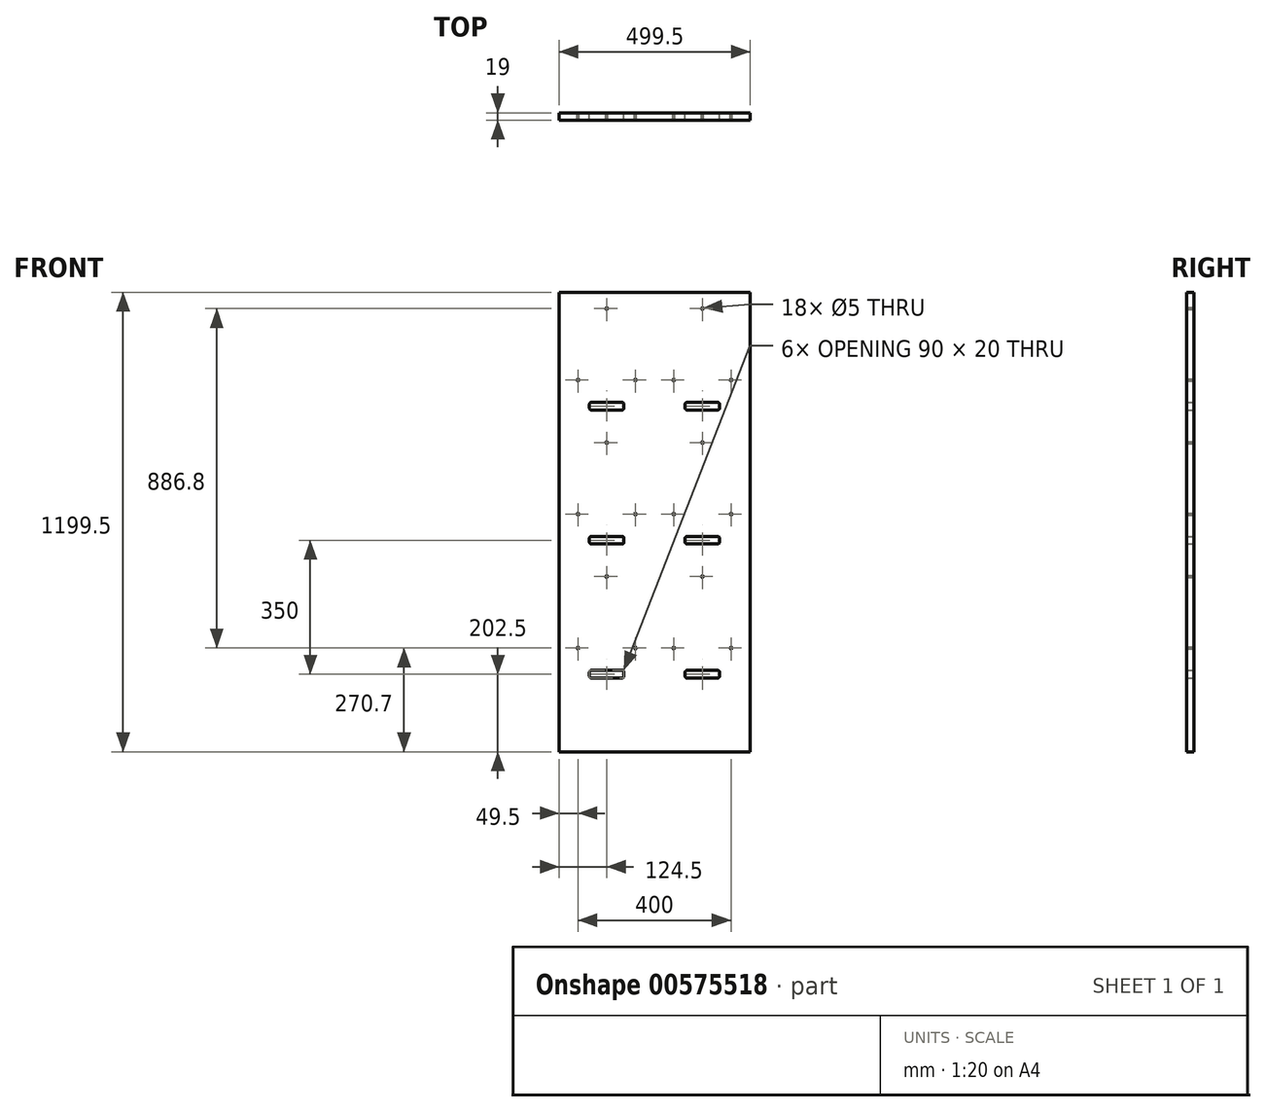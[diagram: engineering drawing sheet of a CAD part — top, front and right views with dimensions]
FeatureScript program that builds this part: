
annotation { "Feature Type Name" : "Feature", "Feature Type Description" : "" }
export const myFeature = defineFeature(function(context is Context, id is Id, definition is map)
    precondition{}
    {
        {
            var Q0;
            Q0=qCreatedBy(makeId("Front.planeOp"),FACE);
            var sketch = newSketch(context, id + "F0", { "sketchPlane" : qUnion([Q0])});
            skLineSegment(sketch, "E0.bottom", {"start": v(0, 0) * mm, "end": v(1000, 0) * mm, "construction": true});
            skLineSegment(sketch, "E0.left", {"start": v(0, 0) * mm, "end": v(0, 1590) * mm, "construction": true});
            skLineSegment(sketch, "E0.right", {"start": v(1000, 0) * mm, "end": v(1000, 1590) * mm, "construction": true});
            skLineSegment(sketch, "E1", {"start": v(500, 1590) * mm, "end": v(500, 0) * mm, "construction": true});
            skLineSegment(sketch, "E2.bottom", {"start": v(0, 1590) * mm, "end": v(1000, 1590) * mm, "construction": true});
            skLineSegment(sketch, "E2.left", {"start": v(0, 1590) * mm, "end": v(0, 290) * mm, "construction": true});
            skSolve(sketch);
        }
        {
            var Q0;
            Q0=qCreatedBy(makeId("Front.planeOp"),FACE);
            var sketch = newSketch(context, id + "F1", { "sketchPlane" : qUnion([Q0])});
            skLineSegment(sketch, "E3.bottom", {"start": v(0, 1590) * mm, "end": v(499.5, 1590) * mm});
            skLineSegment(sketch, "E3.top", {"start": v(0, 390.5) * mm, "end": v(499.5, 390.5) * mm});
            skLineSegment(sketch, "E3.left", {"start": v(0, 1590) * mm, "end": v(0, 390.5) * mm});
            skLineSegment(sketch, "E3.right", {"start": v(499.5, 1590) * mm, "end": v(499.5, 390.5) * mm});
            skLineSegment(sketch, "E4", {"start": v(125, 1590) * mm, "end": v(125, 390.5) * mm, "construction": true});
            skLineSegment(sketch, "E5", {"start": v(375, 1590) * mm, "end": v(375, 390.5) * mm, "construction": true});
            skCircle(sketch, "E6", {"center": v(125, 1548) * mm, "radius": 2.5 * mm});
            skCircle(sketch, "E7", {"center": v(50, 1361.2) * mm, "radius": 2.5 * mm});
            skCircle(sketch, "E8.MirrorC", {"center": v(200, 1361.2) * mm, "radius": 2.5 * mm});
            skLineSegment(sketch, "E9.bottom", {"start": v(165, 1283) * mm, "end": v(85, 1283) * mm});
            skLineSegment(sketch, "E9.top", {"start": v(165, 1303) * mm, "end": v(85, 1303) * mm});
            skLineSegment(sketch, "E9.left", {"start": v(170, 1288) * mm, "end": v(170, 1298) * mm});
            skLineSegment(sketch, "E9.right", {"start": v(80, 1288) * mm, "end": v(80, 1298) * mm});
            skPoint(sketch, "E9.middle", {"position": v(125, 1293) * mm});
            skPoint(sketch, "E10.visualSharp", {"position": v(80, 1303) * mm});
            skArc(sketch, "E10.filletArc", {"start": v(85, 1303) * mm, "mid": v(81.46, 1301.54) * mm, "end": v(80, 1298) * mm});
            skPoint(sketch, "E11.visualSharp", {"position": v(80, 1283) * mm});
            skArc(sketch, "E11.filletArc", {"start": v(80, 1288) * mm, "mid": v(81.46, 1284.46) * mm, "end": v(85, 1283) * mm});
            skPoint(sketch, "E12.visualSharp", {"position": v(170, 1283) * mm});
            skArc(sketch, "E12.filletArc", {"start": v(165, 1283) * mm, "mid": v(168.54, 1284.46) * mm, "end": v(170, 1288) * mm});
            skPoint(sketch, "E13.visualSharp", {"position": v(170, 1303) * mm});
            skArc(sketch, "E13.filletArc", {"start": v(170, 1298) * mm, "mid": v(168.54, 1301.54) * mm, "end": v(165, 1303) * mm});
            skLineSegment(sketch, "E14.0.1.0", {"start": v(165, 953) * mm, "end": v(85, 953) * mm});
            skPoint(sketch, "E14.0.1.1", {"position": v(125, 943) * mm});
            skPoint(sketch, "E14.0.1.2", {"position": v(80, 953) * mm});
            skPoint(sketch, "E14.0.1.3", {"position": v(80, 933) * mm});
            skPoint(sketch, "E14.0.1.4", {"position": v(170, 953) * mm});
            skLineSegment(sketch, "E14.0.1.5", {"start": v(165, 933) * mm, "end": v(85, 933) * mm});
            skPoint(sketch, "E14.0.1.6", {"position": v(170, 933) * mm});
            skCircle(sketch, "E14.0.1.7", {"center": v(125, 1198) * mm, "radius": 2.5 * mm});
            skCircle(sketch, "E14.0.1.8", {"center": v(200, 1011.2) * mm, "radius": 2.5 * mm});
            skCircle(sketch, "E14.0.1.9", {"center": v(50, 1011.2) * mm, "radius": 2.5 * mm});
            skArc(sketch, "E14.0.1.10", {"start": v(170, 948) * mm, "mid": v(168.54, 951.54) * mm, "end": v(165, 953) * mm});
            skArc(sketch, "E14.0.1.11", {"start": v(165, 933) * mm, "mid": v(168.54, 934.46) * mm, "end": v(170, 938) * mm});
            skArc(sketch, "E14.0.1.12", {"start": v(85, 953) * mm, "mid": v(81.46, 951.54) * mm, "end": v(80, 948) * mm});
            skLineSegment(sketch, "E14.0.1.13", {"start": v(170, 938) * mm, "end": v(170, 948) * mm});
            skLineSegment(sketch, "E14.0.1.14", {"start": v(80, 938) * mm, "end": v(80, 948) * mm});
            skArc(sketch, "E14.0.1.15", {"start": v(80, 938) * mm, "mid": v(81.46, 934.46) * mm, "end": v(85, 933) * mm});
            skLineSegment(sketch, "E14.0.2.0", {"start": v(165, 603) * mm, "end": v(85, 603) * mm});
            skPoint(sketch, "E14.0.2.1", {"position": v(125, 593) * mm});
            skPoint(sketch, "E14.0.2.2", {"position": v(80, 603) * mm});
            skPoint(sketch, "E14.0.2.3", {"position": v(80, 583) * mm});
            skPoint(sketch, "E14.0.2.4", {"position": v(170, 603) * mm});
            skLineSegment(sketch, "E14.0.2.5", {"start": v(165, 583) * mm, "end": v(85, 583) * mm});
            skPoint(sketch, "E14.0.2.6", {"position": v(170, 583) * mm});
            skCircle(sketch, "E14.0.2.7", {"center": v(125, 848) * mm, "radius": 2.5 * mm});
            skCircle(sketch, "E14.0.2.8", {"center": v(200, 661.2) * mm, "radius": 2.5 * mm});
            skCircle(sketch, "E14.0.2.9", {"center": v(50, 661.2) * mm, "radius": 2.5 * mm});
            skArc(sketch, "E14.0.2.10", {"start": v(170, 598) * mm, "mid": v(168.54, 601.54) * mm, "end": v(165, 603) * mm});
            skArc(sketch, "E14.0.2.11", {"start": v(165, 583) * mm, "mid": v(168.54, 584.46) * mm, "end": v(170, 588) * mm});
            skArc(sketch, "E14.0.2.12", {"start": v(85, 603) * mm, "mid": v(81.46, 601.54) * mm, "end": v(80, 598) * mm});
            skLineSegment(sketch, "E14.0.2.13", {"start": v(170, 588) * mm, "end": v(170, 598) * mm});
            skLineSegment(sketch, "E14.0.2.14", {"start": v(80, 588) * mm, "end": v(80, 598) * mm});
            skArc(sketch, "E14.0.2.15", {"start": v(80, 588) * mm, "mid": v(81.46, 584.46) * mm, "end": v(85, 583) * mm});
            skLineSegment(sketch, "E14.1.0.0", {"start": v(415, 1303) * mm, "end": v(335, 1303) * mm});
            skPoint(sketch, "E14.1.0.1", {"position": v(375, 1293) * mm});
            skPoint(sketch, "E14.1.0.2", {"position": v(330, 1303) * mm});
            skPoint(sketch, "E14.1.0.3", {"position": v(330, 1283) * mm});
            skPoint(sketch, "E14.1.0.4", {"position": v(420, 1303) * mm});
            skLineSegment(sketch, "E14.1.0.5", {"start": v(415, 1283) * mm, "end": v(335, 1283) * mm});
            skPoint(sketch, "E14.1.0.6", {"position": v(420, 1283) * mm});
            skCircle(sketch, "E14.1.0.7", {"center": v(375, 1548) * mm, "radius": 2.5 * mm});
            skCircle(sketch, "E14.1.0.8", {"center": v(450, 1361.2) * mm, "radius": 2.5 * mm});
            skCircle(sketch, "E14.1.0.9", {"center": v(300, 1361.2) * mm, "radius": 2.5 * mm});
            skArc(sketch, "E14.1.0.10", {"start": v(420, 1298) * mm, "mid": v(418.54, 1301.54) * mm, "end": v(415, 1303) * mm});
            skArc(sketch, "E14.1.0.11", {"start": v(415, 1283) * mm, "mid": v(418.54, 1284.46) * mm, "end": v(420, 1288) * mm});
            skArc(sketch, "E14.1.0.12", {"start": v(335, 1303) * mm, "mid": v(331.46, 1301.54) * mm, "end": v(330, 1298) * mm});
            skLineSegment(sketch, "E14.1.0.13", {"start": v(420, 1288) * mm, "end": v(420, 1298) * mm});
            skLineSegment(sketch, "E14.1.0.14", {"start": v(330, 1288) * mm, "end": v(330, 1298) * mm});
            skArc(sketch, "E14.1.0.15", {"start": v(330, 1288) * mm, "mid": v(331.46, 1284.46) * mm, "end": v(335, 1283) * mm});
            skLineSegment(sketch, "E14.1.1.0", {"start": v(415, 953) * mm, "end": v(335, 953) * mm});
            skPoint(sketch, "E14.1.1.1", {"position": v(375, 943) * mm});
            skPoint(sketch, "E14.1.1.2", {"position": v(330, 953) * mm});
            skPoint(sketch, "E14.1.1.3", {"position": v(330, 933) * mm});
            skPoint(sketch, "E14.1.1.4", {"position": v(420, 953) * mm});
            skLineSegment(sketch, "E14.1.1.5", {"start": v(415, 933) * mm, "end": v(335, 933) * mm});
            skPoint(sketch, "E14.1.1.6", {"position": v(420, 933) * mm});
            skCircle(sketch, "E14.1.1.7", {"center": v(375, 1198) * mm, "radius": 2.5 * mm});
            skCircle(sketch, "E14.1.1.8", {"center": v(450, 1011.2) * mm, "radius": 2.5 * mm});
            skCircle(sketch, "E14.1.1.9", {"center": v(300, 1011.2) * mm, "radius": 2.5 * mm});
            skArc(sketch, "E14.1.1.10", {"start": v(420, 948) * mm, "mid": v(418.54, 951.54) * mm, "end": v(415, 953) * mm});
            skArc(sketch, "E14.1.1.11", {"start": v(415, 933) * mm, "mid": v(418.54, 934.46) * mm, "end": v(420, 938) * mm});
            skArc(sketch, "E14.1.1.12", {"start": v(335, 953) * mm, "mid": v(331.46, 951.54) * mm, "end": v(330, 948) * mm});
            skLineSegment(sketch, "E14.1.1.13", {"start": v(420, 938) * mm, "end": v(420, 948) * mm});
            skLineSegment(sketch, "E14.1.1.14", {"start": v(330, 938) * mm, "end": v(330, 948) * mm});
            skArc(sketch, "E14.1.1.15", {"start": v(330, 938) * mm, "mid": v(331.46, 934.46) * mm, "end": v(335, 933) * mm});
            skLineSegment(sketch, "E14.1.2.0", {"start": v(415, 603) * mm, "end": v(335, 603) * mm});
            skPoint(sketch, "E14.1.2.1", {"position": v(375, 593) * mm});
            skPoint(sketch, "E14.1.2.2", {"position": v(330, 603) * mm});
            skPoint(sketch, "E14.1.2.3", {"position": v(330, 583) * mm});
            skPoint(sketch, "E14.1.2.4", {"position": v(420, 603) * mm});
            skLineSegment(sketch, "E14.1.2.5", {"start": v(415, 583) * mm, "end": v(335, 583) * mm});
            skPoint(sketch, "E14.1.2.6", {"position": v(420, 583) * mm});
            skCircle(sketch, "E14.1.2.7", {"center": v(375, 848) * mm, "radius": 2.5 * mm});
            skCircle(sketch, "E14.1.2.8", {"center": v(450, 661.2) * mm, "radius": 2.5 * mm});
            skCircle(sketch, "E14.1.2.9", {"center": v(300, 661.2) * mm, "radius": 2.5 * mm});
            skArc(sketch, "E14.1.2.10", {"start": v(420, 598) * mm, "mid": v(418.54, 601.54) * mm, "end": v(415, 603) * mm});
            skArc(sketch, "E14.1.2.11", {"start": v(415, 583) * mm, "mid": v(418.54, 584.46) * mm, "end": v(420, 588) * mm});
            skArc(sketch, "E14.1.2.12", {"start": v(335, 603) * mm, "mid": v(331.46, 601.54) * mm, "end": v(330, 598) * mm});
            skLineSegment(sketch, "E14.1.2.13", {"start": v(420, 588) * mm, "end": v(420, 598) * mm});
            skLineSegment(sketch, "E14.1.2.14", {"start": v(330, 588) * mm, "end": v(330, 598) * mm});
            skArc(sketch, "E14.1.2.15", {"start": v(330, 588) * mm, "mid": v(331.46, 584.46) * mm, "end": v(335, 583) * mm});
            skLineSegment(sketch, "E14.direction1", {"start": v(80, 1283) * mm, "end": v(330, 1283) * mm, "construction": true});
            skLineSegment(sketch, "E14.direction2", {"start": v(80, 1283) * mm, "end": v(80, 933) * mm, "construction": true});
            skLineSegment(sketch, "E15.MirrorCS", {"start": v(580, 938) * mm, "end": v(580, 948) * mm});
            skLineSegment(sketch, "E16.MirrorCS", {"start": v(580, 1288) * mm, "end": v(580, 1298) * mm});
            skArc(sketch, "E17.MirrorCS", {"start": v(585, 583) * mm, "mid": v(581.46, 584.46) * mm, "end": v(580, 588) * mm});
            skLineSegment(sketch, "E18.MirrorCS", {"start": v(835, 1283) * mm, "end": v(915, 1283) * mm});
            skArc(sketch, "E19.MirrorCS", {"start": v(830, 598) * mm, "mid": v(831.46, 601.54) * mm, "end": v(835, 603) * mm});
            skLineSegment(sketch, "E20.MirrorCS", {"start": v(830, 588) * mm, "end": v(830, 598) * mm});
            skArc(sketch, "E21.MirrorCS", {"start": v(830, 948) * mm, "mid": v(831.46, 951.54) * mm, "end": v(835, 953) * mm});
            skArc(sketch, "E22.MirrorCS", {"start": v(830, 1298) * mm, "mid": v(831.46, 1301.54) * mm, "end": v(835, 1303) * mm});
            skLineSegment(sketch, "E23.MirrorCS", {"start": v(830, 938) * mm, "end": v(830, 948) * mm});
            skArc(sketch, "E24.MirrorCS", {"start": v(580, 948) * mm, "mid": v(581.46, 951.54) * mm, "end": v(585, 953) * mm});
            skArc(sketch, "E25.MirrorCS", {"start": v(915, 1303) * mm, "mid": v(918.54, 1301.54) * mm, "end": v(920, 1298) * mm});
            skArc(sketch, "E26.MirrorCS", {"start": v(580, 1298) * mm, "mid": v(581.46, 1301.54) * mm, "end": v(585, 1303) * mm});
            skArc(sketch, "E27.MirrorCS", {"start": v(580, 598) * mm, "mid": v(581.46, 601.54) * mm, "end": v(585, 603) * mm});
            skArc(sketch, "E28.MirrorCS", {"start": v(835, 1283) * mm, "mid": v(831.46, 1284.46) * mm, "end": v(830, 1288) * mm});
            skLineSegment(sketch, "E29.MirrorCS", {"start": v(835, 1303) * mm, "end": v(915, 1303) * mm});
            skArc(sketch, "E30.MirrorCS", {"start": v(835, 583) * mm, "mid": v(831.46, 584.46) * mm, "end": v(830, 588) * mm});
            skLineSegment(sketch, "E31.MirrorCS", {"start": v(830, 1288) * mm, "end": v(830, 1298) * mm});
            skLineSegment(sketch, "E32.MirrorCS", {"start": v(580, 588) * mm, "end": v(580, 598) * mm});
            skArc(sketch, "E33.MirrorCS", {"start": v(835, 933) * mm, "mid": v(831.46, 934.46) * mm, "end": v(830, 938) * mm});
            skLineSegment(sketch, "E34.MirrorCS", {"start": v(920, 1288) * mm, "end": v(920, 1298) * mm});
            skArc(sketch, "E35.MirrorCS", {"start": v(920, 1288) * mm, "mid": v(918.54, 1284.46) * mm, "end": v(915, 1283) * mm});
            skArc(sketch, "E36.MirrorCS", {"start": v(585, 933) * mm, "mid": v(581.46, 934.46) * mm, "end": v(580, 938) * mm});
            skArc(sketch, "E37.MirrorCS", {"start": v(585, 1283) * mm, "mid": v(581.46, 1284.46) * mm, "end": v(580, 1288) * mm});
            skLineSegment(sketch, "E38.MirrorCS", {"start": v(585, 1283) * mm, "end": v(665, 1283) * mm});
            skArc(sketch, "E39.MirrorCS", {"start": v(670, 1288) * mm, "mid": v(668.54, 1284.46) * mm, "end": v(665, 1283) * mm});
            skLineSegment(sketch, "E40.MirrorCS", {"start": v(670, 1288) * mm, "end": v(670, 1298) * mm});
            skArc(sketch, "E41.MirrorCS", {"start": v(665, 953) * mm, "mid": v(668.54, 951.54) * mm, "end": v(670, 948) * mm});
            skArc(sketch, "E42.MirrorCS", {"start": v(665, 1303) * mm, "mid": v(668.54, 1301.54) * mm, "end": v(670, 1298) * mm});
            skArc(sketch, "E43.MirrorCS", {"start": v(915, 603) * mm, "mid": v(918.54, 601.54) * mm, "end": v(920, 598) * mm});
            skLineSegment(sketch, "E44.MirrorCS", {"start": v(585, 1303) * mm, "end": v(665, 1303) * mm});
            skLineSegment(sketch, "E45.MirrorCS", {"start": v(920, 938) * mm, "end": v(920, 948) * mm});
            skLineSegment(sketch, "E46.MirrorCS", {"start": v(585, 953) * mm, "end": v(665, 953) * mm});
            skArc(sketch, "E47.MirrorCS", {"start": v(920, 588) * mm, "mid": v(918.54, 584.46) * mm, "end": v(915, 583) * mm});
            skArc(sketch, "E48.MirrorCS", {"start": v(920, 938) * mm, "mid": v(918.54, 934.46) * mm, "end": v(915, 933) * mm});
            skLineSegment(sketch, "E49.MirrorCS", {"start": v(835, 583) * mm, "end": v(915, 583) * mm});
            skArc(sketch, "E50.MirrorCS", {"start": v(915, 953) * mm, "mid": v(918.54, 951.54) * mm, "end": v(920, 948) * mm});
            skLineSegment(sketch, "E51.MirrorCS", {"start": v(670, 588) * mm, "end": v(670, 598) * mm});
            skLineSegment(sketch, "E52.MirrorCS", {"start": v(670, 938) * mm, "end": v(670, 948) * mm});
            skArc(sketch, "E53.MirrorCS", {"start": v(670, 588) * mm, "mid": v(668.54, 584.46) * mm, "end": v(665, 583) * mm});
            skLineSegment(sketch, "E54.MirrorCS", {"start": v(585, 603) * mm, "end": v(665, 603) * mm});
            skLineSegment(sketch, "E55.MirrorCS", {"start": v(835, 933) * mm, "end": v(915, 933) * mm});
            skLineSegment(sketch, "E56.MirrorCS", {"start": v(585, 583) * mm, "end": v(665, 583) * mm});
            skArc(sketch, "E57.MirrorCS", {"start": v(665, 603) * mm, "mid": v(668.54, 601.54) * mm, "end": v(670, 598) * mm});
            skArc(sketch, "E58.MirrorCS", {"start": v(670, 938) * mm, "mid": v(668.54, 934.46) * mm, "end": v(665, 933) * mm});
            skLineSegment(sketch, "E59.MirrorCS", {"start": v(835, 953) * mm, "end": v(915, 953) * mm});
            skLineSegment(sketch, "E60.MirrorCS", {"start": v(920, 588) * mm, "end": v(920, 598) * mm});
            skLineSegment(sketch, "E61.MirrorCS", {"start": v(585, 933) * mm, "end": v(665, 933) * mm});
            skLineSegment(sketch, "E62.MirrorCS", {"start": v(835, 603) * mm, "end": v(915, 603) * mm});
            skCircle(sketch, "E63.MirrorC", {"center": v(800, 661.2) * mm, "radius": 2.5 * mm});
            skCircle(sketch, "E64.MirrorC", {"center": v(950, 1011.2) * mm, "radius": 2.5 * mm});
            skCircle(sketch, "E65.MirrorC", {"center": v(550, 1361.2) * mm, "radius": 2.5 * mm});
            skCircle(sketch, "E66.MirrorC", {"center": v(875, 1548) * mm, "radius": 2.5 * mm});
            skCircle(sketch, "E67.MirrorC", {"center": v(875, 1198) * mm, "radius": 2.5 * mm});
            skCircle(sketch, "E68.MirrorC", {"center": v(875, 848) * mm, "radius": 2.5 * mm});
            skCircle(sketch, "E69.MirrorC", {"center": v(950, 661.2) * mm, "radius": 2.5 * mm});
            skCircle(sketch, "E70.MirrorC", {"center": v(550, 1011.2) * mm, "radius": 2.5 * mm});
            skCircle(sketch, "E71.MirrorC", {"center": v(625, 848) * mm, "radius": 2.5 * mm});
            skCircle(sketch, "E72.MirrorC", {"center": v(700, 1011.2) * mm, "radius": 2.5 * mm});
            skCircle(sketch, "E73.MirrorC", {"center": v(700, 661.2) * mm, "radius": 2.5 * mm});
            skCircle(sketch, "E74.MirrorC", {"center": v(625, 1548) * mm, "radius": 2.5 * mm});
            skCircle(sketch, "E75.MirrorC", {"center": v(800, 1361.2) * mm, "radius": 2.5 * mm});
            skCircle(sketch, "E76.MirrorC", {"center": v(800, 1011.2) * mm, "radius": 2.5 * mm});
            skPoint(sketch, "E77.MirrorP", {"position": v(875, 1293) * mm});
            skCircle(sketch, "E78.MirrorC", {"center": v(700, 1361.2) * mm, "radius": 2.5 * mm});
            skPoint(sketch, "E79.MirrorP", {"position": v(625, 1293) * mm});
            skCircle(sketch, "E80.MirrorC", {"center": v(950, 1361.2) * mm, "radius": 2.5 * mm});
            skPoint(sketch, "E81.MirrorP", {"position": v(920, 1303) * mm});
            skCircle(sketch, "E82.MirrorC", {"center": v(550, 661.2) * mm, "radius": 2.5 * mm});
            skCircle(sketch, "E83.MirrorC", {"center": v(625, 1198) * mm, "radius": 2.5 * mm});
            skLineSegment(sketch, "E84.MirrorCS", {"start": v(920, 1283) * mm, "end": v(920, 933) * mm, "construction": true});
            skPoint(sketch, "E85.MirrorP", {"position": v(580, 603) * mm});
            skPoint(sketch, "E86.MirrorP", {"position": v(625, 943) * mm});
            skPoint(sketch, "E87.MirrorP", {"position": v(580, 953) * mm});
            skPoint(sketch, "E88.MirrorP", {"position": v(670, 953) * mm});
            skPoint(sketch, "E89.MirrorP", {"position": v(830, 603) * mm});
            skPoint(sketch, "E90.MirrorP", {"position": v(580, 1303) * mm});
            skPoint(sketch, "E91.MirrorP", {"position": v(920, 953) * mm});
            skPoint(sketch, "E92.MirrorP", {"position": v(830, 583) * mm});
            skPoint(sketch, "E93.MirrorP", {"position": v(920, 933) * mm});
            skPoint(sketch, "E94.MirrorP", {"position": v(830, 1283) * mm});
            skPoint(sketch, "E95.MirrorP", {"position": v(670, 1303) * mm});
            skPoint(sketch, "E96.MirrorP", {"position": v(580, 1283) * mm});
            skPoint(sketch, "E97.MirrorP", {"position": v(670, 583) * mm});
            skPoint(sketch, "E98.MirrorP", {"position": v(830, 1303) * mm});
            skLineSegment(sketch, "E99.MirrorCS", {"start": v(625, 1590) * mm, "end": v(625, 390.5) * mm, "construction": true});
            skLineSegment(sketch, "E100.MirrorCS", {"start": v(875, 1590) * mm, "end": v(875, 390.5) * mm, "construction": true});
            skLineSegment(sketch, "E101.MirrorCS", {"start": v(920, 1283) * mm, "end": v(670, 1283) * mm, "construction": true});
            skPoint(sketch, "E102.MirrorP", {"position": v(830, 953) * mm});
            skPoint(sketch, "E103.MirrorP", {"position": v(830, 933) * mm});
            skPoint(sketch, "E104.MirrorP", {"position": v(580, 583) * mm});
            skPoint(sketch, "E105.MirrorP", {"position": v(875, 943) * mm});
            skPoint(sketch, "E106.MirrorP", {"position": v(670, 1283) * mm});
            skPoint(sketch, "E107.MirrorP", {"position": v(580, 933) * mm});
            skLineSegment(sketch, "E108.MirrorCS", {"start": v(1000, 1590) * mm, "end": v(1000, 390.5) * mm});
            skPoint(sketch, "E109.MirrorP", {"position": v(625, 593) * mm});
            skLineSegment(sketch, "E110.MirrorCS", {"start": v(1000, 390.5) * mm, "end": v(500.5, 390.5) * mm});
            skPoint(sketch, "E111.MirrorP", {"position": v(875, 593) * mm});
            skPoint(sketch, "E112.MirrorP", {"position": v(920, 583) * mm});
            skLineSegment(sketch, "E113.MirrorCS", {"start": v(1000, 1590) * mm, "end": v(500.5, 1590) * mm});
            skPoint(sketch, "E114.MirrorP", {"position": v(920, 603) * mm});
            skPoint(sketch, "E115.MirrorP", {"position": v(670, 603) * mm});
            skPoint(sketch, "E116.MirrorP", {"position": v(670, 933) * mm});
            skPoint(sketch, "E117.MirrorP", {"position": v(920, 1283) * mm});
            skLineSegment(sketch, "E118.MirrorCS", {"start": v(500.5, 1590) * mm, "end": v(500.5, 390.5) * mm});
            skSolve(sketch);
        }
        {
            var Q0;
            Q0=makeQuery(id+"F1.imprint","IMPRINT",FACE,{"disambiguationData":[TD([[makeQuery(id+"F1.imprint","IMPRINT",EDGE,{"derivedFrom":sQuery(id+"F1.wireOp",EDGE,"E15.MirrorCS")}),1.0]])]});
            extrude(context, id + "F2", {"entities" : qUnion([Q0]), "depth" : 19 * mm, "offsetDistance" : 25 * mm});
        }
        {
            var Q0;
            Q0=makeQuery(id+"F2.opExtrude","SWEPT_BODY",BODY,{"disambiguationData":[OSD([sQuery(id+"F1.wireOp",EDGE,"E15.MirrorCS"),sQuery(id+"F1.wireOp",EDGE,"E16.MirrorCS"),sQuery(id+"F1.wireOp",EDGE,"E17.MirrorCS"),sQuery(id+"F1.wireOp",EDGE,"E18.MirrorCS"),sQuery(id+"F1.wireOp",EDGE,"E19.MirrorCS"),sQuery(id+"F1.wireOp",EDGE,"E20.MirrorCS"),sQuery(id+"F1.wireOp",EDGE,"E21.MirrorCS"),sQuery(id+"F1.wireOp",EDGE,"E22.MirrorCS"),sQuery(id+"F1.wireOp",EDGE,"E23.MirrorCS"),sQuery(id+"F1.wireOp",EDGE,"E24.MirrorCS"),sQuery(id+"F1.wireOp",EDGE,"E25.MirrorCS"),sQuery(id+"F1.wireOp",EDGE,"E26.MirrorCS"),sQuery(id+"F1.wireOp",EDGE,"E27.MirrorCS"),sQuery(id+"F1.wireOp",EDGE,"E28.MirrorCS"),sQuery(id+"F1.wireOp",EDGE,"E29.MirrorCS"),sQuery(id+"F1.wireOp",EDGE,"E30.MirrorCS"),sQuery(id+"F1.wireOp",EDGE,"E31.MirrorCS"),sQuery(id+"F1.wireOp",EDGE,"E32.MirrorCS"),sQuery(id+"F1.wireOp",EDGE,"E33.MirrorCS"),sQuery(id+"F1.wireOp",EDGE,"E34.MirrorCS"),sQuery(id+"F1.wireOp",EDGE,"E35.MirrorCS"),sQuery(id+"F1.wireOp",EDGE,"E36.MirrorCS"),sQuery(id+"F1.wireOp",EDGE,"E37.MirrorCS"),sQuery(id+"F1.wireOp",EDGE,"E38.MirrorCS"),sQuery(id+"F1.wireOp",EDGE,"E39.MirrorCS"),sQuery(id+"F1.wireOp",EDGE,"E40.MirrorCS"),sQuery(id+"F1.wireOp",EDGE,"E41.MirrorCS"),sQuery(id+"F1.wireOp",EDGE,"E42.MirrorCS"),sQuery(id+"F1.wireOp",EDGE,"E43.MirrorCS"),sQuery(id+"F1.wireOp",EDGE,"E44.MirrorCS"),sQuery(id+"F1.wireOp",EDGE,"E45.MirrorCS"),sQuery(id+"F1.wireOp",EDGE,"E46.MirrorCS"),sQuery(id+"F1.wireOp",EDGE,"E47.MirrorCS"),sQuery(id+"F1.wireOp",EDGE,"E48.MirrorCS"),sQuery(id+"F1.wireOp",EDGE,"E49.MirrorCS"),sQuery(id+"F1.wireOp",EDGE,"E50.MirrorCS"),sQuery(id+"F1.wireOp",EDGE,"E51.MirrorCS"),sQuery(id+"F1.wireOp",EDGE,"E52.MirrorCS"),sQuery(id+"F1.wireOp",EDGE,"E53.MirrorCS"),sQuery(id+"F1.wireOp",EDGE,"E54.MirrorCS"),sQuery(id+"F1.wireOp",EDGE,"E55.MirrorCS"),sQuery(id+"F1.wireOp",EDGE,"E56.MirrorCS"),sQuery(id+"F1.wireOp",EDGE,"E57.MirrorCS"),sQuery(id+"F1.wireOp",EDGE,"E58.MirrorCS"),sQuery(id+"F1.wireOp",EDGE,"E59.MirrorCS"),sQuery(id+"F1.wireOp",EDGE,"E60.MirrorCS"),sQuery(id+"F1.wireOp",EDGE,"E61.MirrorCS"),sQuery(id+"F1.wireOp",EDGE,"E62.MirrorCS"),sQuery(id+"F1.wireOp",EDGE,"E63.MirrorC"),sQuery(id+"F1.wireOp",EDGE,"E64.MirrorC"),sQuery(id+"F1.wireOp",EDGE,"E65.MirrorC"),sQuery(id+"F1.wireOp",EDGE,"E66.MirrorC"),sQuery(id+"F1.wireOp",EDGE,"E67.MirrorC"),sQuery(id+"F1.wireOp",EDGE,"E68.MirrorC"),sQuery(id+"F1.wireOp",EDGE,"E69.MirrorC"),sQuery(id+"F1.wireOp",EDGE,"E70.MirrorC"),sQuery(id+"F1.wireOp",EDGE,"E71.MirrorC"),sQuery(id+"F1.wireOp",EDGE,"E72.MirrorC"),sQuery(id+"F1.wireOp",EDGE,"E73.MirrorC"),sQuery(id+"F1.wireOp",EDGE,"E74.MirrorC"),sQuery(id+"F1.wireOp",EDGE,"E75.MirrorC"),sQuery(id+"F1.wireOp",EDGE,"E76.MirrorC"),sQuery(id+"F1.wireOp",EDGE,"E78.MirrorC"),sQuery(id+"F1.wireOp",EDGE,"E80.MirrorC"),sQuery(id+"F1.wireOp",EDGE,"E82.MirrorC"),sQuery(id+"F1.wireOp",EDGE,"E83.MirrorC"),sQuery(id+"F1.wireOp",EDGE,"E108.MirrorCS"),sQuery(id+"F1.wireOp",EDGE,"E110.MirrorCS"),sQuery(id+"F1.wireOp",EDGE,"E113.MirrorCS"),sQuery(id+"F1.wireOp",EDGE,"E118.MirrorCS")])]});
            var Q1;
            Q1=makeQuery(id+"F2.opExtrude","CAP_VERTEX",VERTEX,{"disambiguationData":[OSD([sQuery(id+"F1.wireOp",EDGE,"E110.MirrorCS"),sQuery(id+"F1.wireOp",EDGE,"E118.MirrorCS")])],"isStart":true});
            var Q2;
            Q2=sQuery(id+"F0.wireOp",VERTEX,"E0.bottom.start");
            transform(context, id + "F3", {"entities" : qUnion([Q0]), "transformType" : TransformType.TRANSLATION_ENTITY, "oppositeDirectionEntity" : false, "transformLine" : qUnion([Q1, Q2]), "makeCopy" : false});
        }
    });
